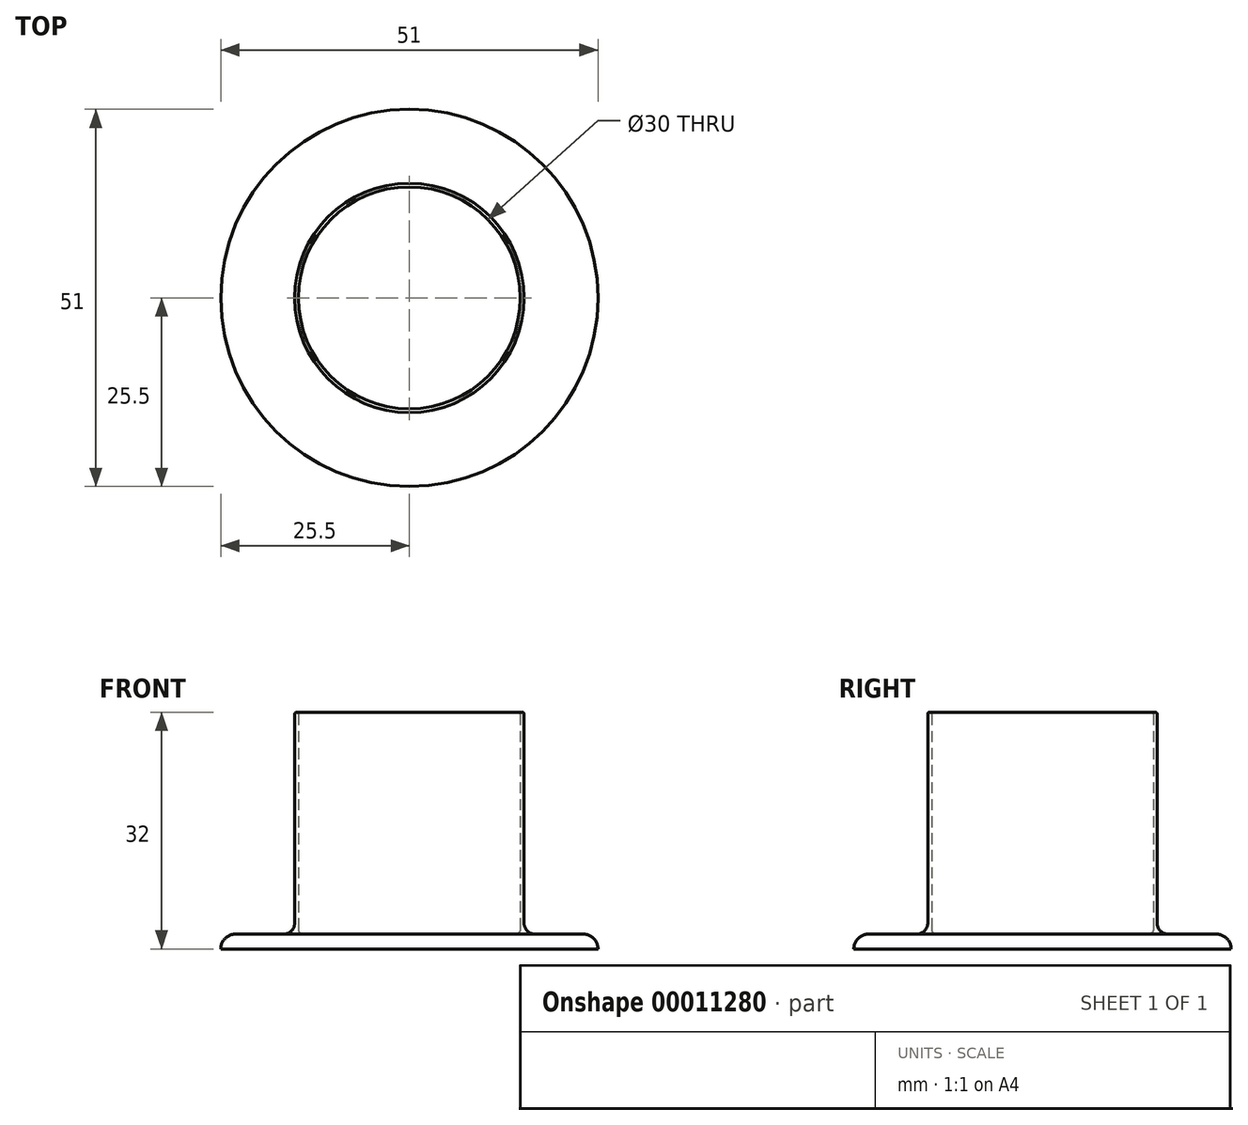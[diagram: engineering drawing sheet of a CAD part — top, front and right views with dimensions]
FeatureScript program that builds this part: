
annotation { "Feature Type Name" : "Feature", "Feature Type Description" : "" }
export const myFeature = defineFeature(function(context is Context, id is Id, definition is map)
    precondition{}
    {
        {
            var Q0;
            Q0=qCreatedBy(makeId("Front.planeOp"),FACE);
            var sketch = newSketch(context, id + "F0", { "sketchPlane" : qUnion([Q0])});
            skLineSegment(sketch, "E0", {"start": v(0, 0) * mm, "end": v(0, 2) * mm});
            skLineSegment(sketch, "E1", {"start": v(0, 2) * mm, "end": v(14.32, 2) * mm});
            skLineSegment(sketch, "E2", {"start": v(15, 2.68) * mm, "end": v(15, 31.75) * mm});
            skLineSegment(sketch, "E3", {"start": v(15.25, 32) * mm, "end": v(15.25, 32) * mm});
            skLineSegment(sketch, "E4", {"start": v(15.5, 31.75) * mm, "end": v(15.5, 3.5) * mm});
            skLineSegment(sketch, "E5", {"start": v(17, 2) * mm, "end": v(23.5, 2) * mm});
            skLineSegment(sketch, "E6", {"start": v(25.5, 0) * mm, "end": v(25.5, 0) * mm});
            skLineSegment(sketch, "E7", {"start": v(25.5, 0) * mm, "end": v(0, 0) * mm});
            skPoint(sketch, "E8.visualSharp", {"position": v(25.5, 2) * mm});
            skArc(sketch, "E8.filletArc", {"start": v(25.5, 0) * mm, "mid": v(24.91, 1.41) * mm, "end": v(23.5, 2) * mm});
            skPoint(sketch, "E9.visualSharp", {"position": v(15.5, 2) * mm});
            skArc(sketch, "E9.filletArc", {"start": v(15.5, 3.5) * mm, "mid": v(15.94, 2.44) * mm, "end": v(17, 2) * mm});
            skPoint(sketch, "E10.visualSharp", {"position": v(15, 2) * mm});
            skArc(sketch, "E10.filletArc", {"start": v(14.32, 2) * mm, "mid": v(14.8, 2.2) * mm, "end": v(15, 2.68) * mm});
            skPoint(sketch, "E11.visualSharp", {"position": v(15, 32) * mm});
            skArc(sketch, "E11.filletArc", {"start": v(15.25, 32) * mm, "mid": v(15.07, 31.93) * mm, "end": v(15, 31.75) * mm});
            skPoint(sketch, "E12.visualSharp", {"position": v(15.5, 32) * mm});
            skArc(sketch, "E12.filletArc", {"start": v(15.5, 31.75) * mm, "mid": v(15.43, 31.93) * mm, "end": v(15.25, 32) * mm});
            skSolve(sketch);
        }
        {
            var Q0;
            Q0 = qSketchRegion(id + "F0", true);
            var Q1;
            Q1=sQuery(id+"F0.wireOp",EDGE,"E0");
            revolve(context, id + "F1", {"entities" : qUnion([Q0]), "axis" : qUnion([Q1]), "revolveType" : RevolveType.FULL});
        }
    });
